# Revit family: 201ea584-255e-427a-b544-9d0f85d0b6e6
name_source: partatom
category: Doors
revit_build: Autodesk Revit 2014 (Build: 20130308_1515(x64)
units: mm (PartAtom-declared; Revit-internal decimal feet)

## types (4) — shared parameters
AAMA Designation = as Specified
Air Infiltration = as Specified
Analytic Construction = <None>
Fire Rating = As Specified
Frame Depth = 0' - 4 1/2"
Function = Interior
Heat Transfer Coefficient (U) = 1 BTU/(h·ft²·°F)
Manufacturer = Western Window Systems
Manufacturer Fax = 602-243-3119
Manufacturer Website = https://www.westernwindowsystems.com
Miami Dade Conformance = as Specified
Model = 900 Hinged Door
Operation = as Specified
Panel Thickness = 0' - 1 3/4"
Product Data = http://www.arcat.com
Product Properties = https://www.westernwindowsystems.com
R = 0.0000 (h·ft²·°F)/BTU
RO Offset = 0' - 0 1/2"
Sales Information = https://www.westernwindowsystems.com
Standards Conformance = as Specified
Structural Test Pressure = as Specified
Thermal Resistance (R) = 0.0000 (h·ft²·°F)/BTU
Thickness = 0' - 0"
U = 1 BTU/(h·ft²·°F)
URL = https://www.westernwindowsystems.com
Wall Closure = By host
Water Penetration = as Specified
zero-valued in all types: Expected Lifespan (Years), Maintenance Schedule (Months), SHGC, Solar Heat Gain Coefficient, VLT, Visual Light Transmittance, Warranty Duration (Years)

## per-type parameters (varying)
| type | Description | Door has Narrow Stile | Flip Nailing Fin | Maximum Size |
| Medium Stile Outswing | Western Window Aluminum Outswing Door - 900 Series as Specified | No | Yes | 45'' Width  ;  121.5'' Height |
| Medium Stile Inswing | Western Window Aluminum Inswing Door - 900 Series as Specified | No | No | 45'' Width  ;  121.5'' Height |
| Narrow Stile Outswing | Western Window Aluminum Outswing Door - 900 Series as Specified | Yes | Yes | 39'' Width  ;  109.5'' Height |
| Narrow Stile Inswing | Western Window Aluminum Inswing Door - 900 Series as Specified | Yes | No | 39'' Width  ;  109.5'' Height |

## geometry (parser evidence)
native form markers: Sweep x10
no freeform markers — native parametric forms only
